# Revit family: 3-115-xx Temple Fan e
name_source: partatom
category: Generic Models
units: mm (PartAtom-declared; Revit-internal decimal feet)

## family parameters
Always vertical = Yes
Can host rebar = No
Cut with Voids When Loaded = No
Host = Ceiling
Part Type = Normal
Room Calculation Point = No
Round Connector Dimension = Use Diameter
Shared = No

## types (3) — shared parameters
Main Diffuser = Matte White Acrylic
Manufacturer = Oxygen - Lighting & Fans
Model = 3-115-xx Temple Fan
References = Ref. 3 = 120 V / Ref. 37 = 277 V
URL = www.oxygenlighting.ocm
Voltage = 120 V
Voltage input = 120 V or 277 V - 50/60 Hz
zero-valued in all types: Default Elevation

## per-type parameters (varying)
| type | Blade Finish | Metal Finish |
| 3-115-15 / Black - Weathered Gray blades | Weathered Gray Blades | 15 - Black |
| 3-115-24 / Satin Nickel - Weathered Gray blades | Weathered Gray Blades | 24 - Satin Nickel |
| 3-115-640 / Aged Brass - White Blades | 6 - White | 40 - Aged Brass |

## geometry (parser evidence)
native form markers: Sweep x6
no freeform markers — native parametric forms only
